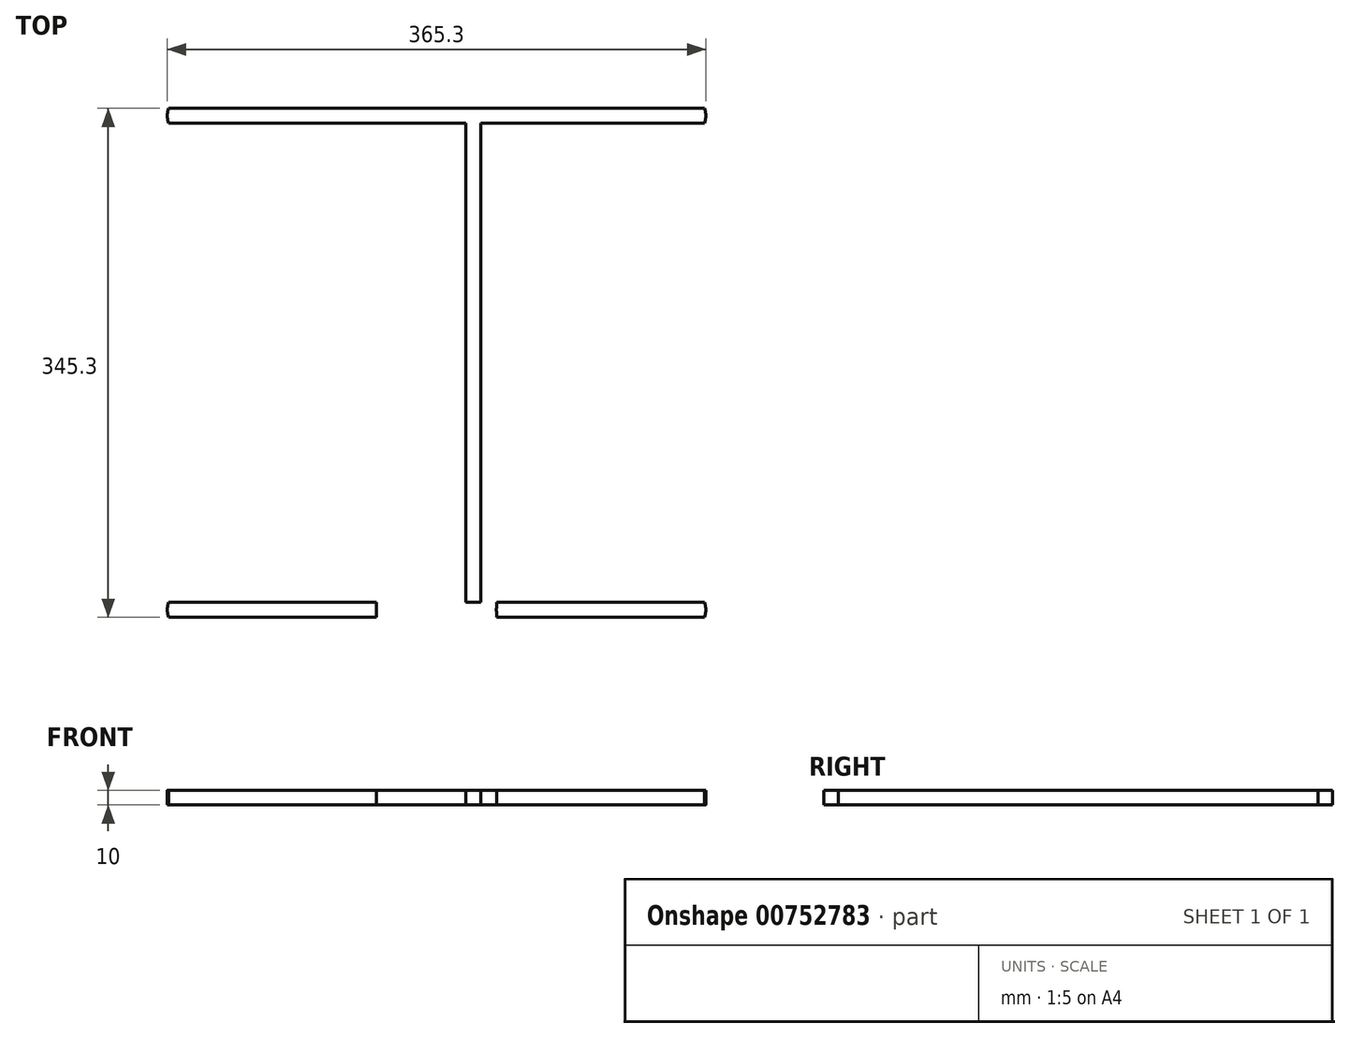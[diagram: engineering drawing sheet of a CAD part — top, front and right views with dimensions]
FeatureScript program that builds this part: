
annotation { "Feature Type Name" : "Feature", "Feature Type Description" : "" }
export const myFeature = defineFeature(function(context is Context, id is Id, definition is map)
    precondition{}
    {
        {
            var Q0;
            Q0=qCreatedBy(makeId("Top.planeOp"),FACE);
            var sketch = newSketch(context, id + "F0", { "sketchPlane" : qUnion([Q0])});
            skLineSegment(sketch, "E0.bottom", {"start": v(-30, 162.65) * mm, "end": v(30, 162.65) * mm});
            skLineSegment(sketch, "E0.top", {"start": v(-30, -162.65) * mm, "end": v(30, -162.65) * mm});
            skLineSegment(sketch, "E0.left", {"start": v(-30, 162.65) * mm, "end": v(-30, -162.65) * mm});
            skLineSegment(sketch, "E0.right", {"start": v(30, 162.65) * mm, "end": v(30, -162.65) * mm});
            skPoint(sketch, "E0.middle", {"position": v(0, 0) * mm});
            skLineSegment(sketch, "E1", {"start": v(0, 164.7) * mm, "end": v(0, 162.65) * mm, "construction": true});
            skPoint(sketch, "E1.startSnap0", {"position": v(0, 162.65) * mm});
            skPoint(sketch, "E1.endSnap0", {"position": v(0, -162.65) * mm});
            skLineSegment(sketch, "E2.bottom", {"start": v(0, 162.65) * mm, "end": v(182.65, 162.65) * mm});
            skLineSegment(sketch, "E2.top", {"start": v(0, 172.65) * mm, "end": v(182.65, 172.65) * mm});
            skLineSegment(sketch, "E2.left", {"start": v(0, 162.65) * mm, "end": v(0, 172.65) * mm});
            skLineSegment(sketch, "E2.right", {"start": v(182.65, 162.65) * mm, "end": v(182.65, 172.65) * mm});
            skLineSegment(sketch, "E3", {"start": v(-190.93, 0) * mm, "end": v(-190.22, 0) * mm, "construction": true});
            skPoint(sketch, "E3.endSnap0", {"position": v(-30, 0) * mm});
            skLineSegment(sketch, "E4.MirrorCS", {"start": v(0, 172.65) * mm, "end": v(-182.65, 172.65) * mm});
            skLineSegment(sketch, "E5.MirrorCS", {"start": v(0, 162.65) * mm, "end": v(-182.65, 162.65) * mm});
            skLineSegment(sketch, "E6.MirrorCS", {"start": v(-182.65, 162.65) * mm, "end": v(-182.65, 172.65) * mm});
            skLineSegment(sketch, "E7.MirrorCS", {"start": v(0, -172.65) * mm, "end": v(-182.65, -172.65) * mm});
            skLineSegment(sketch, "E8.MirrorCS", {"start": v(0, -162.65) * mm, "end": v(-182.65, -162.65) * mm});
            skLineSegment(sketch, "E9.MirrorCS", {"start": v(0, -172.65) * mm, "end": v(182.65, -172.65) * mm});
            skLineSegment(sketch, "E10.MirrorCS", {"start": v(0, -162.65) * mm, "end": v(182.65, -162.65) * mm});
            skLineSegment(sketch, "E11.MirrorCS", {"start": v(182.65, -162.65) * mm, "end": v(182.65, -172.65) * mm});
            skLineSegment(sketch, "E12.MirrorCS", {"start": v(-182.65, -162.65) * mm, "end": v(-182.65, -172.65) * mm});
            skLineSegment(sketch, "E13", {"start": v(170.21, 167.65) * mm, "end": v(167.65, 167.65) * mm, "construction": true});
            skCircle(sketch, "E14", {"center": v(-167.65, 167.65) * mm, "radius": 127 * mm});
            skCircle(sketch, "E15.MirrorC", {"center": v(-167.65, -167.65) * mm, "radius": 127 * mm});
            skCircle(sketch, "E16.MirrorC", {"center": v(167.65, 167.65) * mm, "radius": 127 * mm});
            skCircle(sketch, "E17.MirrorC", {"center": v(167.65, -167.65) * mm, "radius": 127 * mm});
            skLineSegment(sketch, "E18.bottom", {"start": v(-30, 162.65) * mm, "end": v(-20, 162.65) * mm});
            skLineSegment(sketch, "E18.top", {"start": v(-30, -162.65) * mm, "end": v(-20, -162.65) * mm});
            skLineSegment(sketch, "E18.right", {"start": v(-20, 162.65) * mm, "end": v(-20, -162.65) * mm});
            skLineSegment(sketch, "E19.MirrorCS", {"start": v(20, 162.65) * mm, "end": v(20, -162.65) * mm});
            skCircle(sketch, "E20", {"center": v(167.65, -167.65) * mm, "radius": 15 * mm});
            skCircle(sketch, "E21.MirrorC", {"center": v(-167.65, -167.65) * mm, "radius": 15 * mm});
            skLineSegment(sketch, "E22.MirrorCS", {"start": v(190.93, 0) * mm, "end": v(190.22, 0) * mm, "construction": true});
            skCircle(sketch, "E23.MirrorC", {"center": v(167.65, 167.65) * mm, "radius": 15 * mm});
            skCircle(sketch, "E24.MirrorC", {"center": v(-167.65, 167.65) * mm, "radius": 15 * mm});
            skLineSegment(sketch, "E25.trimOffspring", {"start": v(-30, 0) * mm, "end": v(-20, 0) * mm, "construction": true});
            skLineSegment(sketch, "E26.trimOffspring", {"start": v(20, 0) * mm, "end": v(30, 0) * mm, "construction": true});
            skLineSegment(sketch, "E27.trimOffspring", {"start": v(0, -162.65) * mm, "end": v(0, -172.65) * mm, "construction": true});
            skLineSegment(sketch, "E28.trimOffspring", {"start": v(30, 0) * mm, "end": v(20, 0) * mm, "construction": true});
            skPoint(sketch, "E29.orphan", {"position": v(0, -175.9) * mm});
            skPoint(sketch, "E30.trimOffspring.end.orphan", {"position": v(190.22, 0) * mm});
            skLineSegment(sketch, "E31.trimOffspring", {"start": v(-20, 0) * mm, "end": v(-30, 0) * mm, "construction": true});
            skLineSegment(sketch, "E32.trimOffspring", {"start": v(0, 0) * mm, "end": v(30, 0) * mm, "construction": true});
            skPoint(sketch, "E33.orphan", {"position": v(-182.65, 167.65) * mm});
            skPoint(sketch, "E34.orphan", {"position": v(182.65, 167.65) * mm});
            skLineSegment(sketch, "E35", {"start": v(0, -162.65) * mm, "end": v(0, -188.9) * mm, "construction": true});
            skCircle(sketch, "E36", {"center": v(0, 0) * mm, "radius": 238.4 * mm, "construction": true});
            skSolve(sketch);
        }
        {
            var Q0;
            {var subQ0=sQuery(id+"F0.wireOp",EDGE,"E15.MirrorC");var subQ1=sQuery(id+"F0.wireOp",EDGE,"E7.MirrorCS");var subQ2=makeQuery(id+"F0.imprint","INTERSECT",VERTEX,{"derivedFrom":[subQ1,subQ0]});Q0=makeQuery(id+"F0.imprint","IMPRINT",FACE,{"disambiguationData":[TD([[makeQuery(id+"F0.imprint","IMPRINT",EDGE,{"disambiguationData":[TD([[subQ2,-1.0]])],"derivedFrom":subQ1}),-1.0]])]});}
            var Q1;
            {var subQ8=sQuery(id+"F0.wireOp",EDGE,"E18.top");Q1=makeQuery(id+"F0.imprint","IMPRINT",FACE,{"disambiguationData":[TD([[makeQuery(id+"F0.imprint","IMPRINT",EDGE,{"derivedFrom":subQ8}),-1.0]])]});}
            var Q2;
            {var subQ0=sQuery(id+"F0.wireOp",EDGE,"E17.MirrorC");var subQ1=sQuery(id+"F0.wireOp",EDGE,"E9.MirrorCS");var subQ2=makeQuery(id+"F0.imprint","INTERSECT",VERTEX,{"derivedFrom":[subQ1,subQ0]});Q2=makeQuery(id+"F0.imprint","IMPRINT",FACE,{"disambiguationData":[TD([[makeQuery(id+"F0.imprint","IMPRINT",EDGE,{"disambiguationData":[TD([[subQ2,-1.0]])],"derivedFrom":subQ1}),1.0]])]});}
            var Q3;
            {var subQ0=sQuery(id+"F0.wireOp",EDGE,"E20");var subQ1=sQuery(id+"F0.wireOp",EDGE,"E9.MirrorCS");var subQ2=makeQuery(id+"F0.imprint","INTERSECT",VERTEX,{"disambiguationData":[OD(0.0)],"derivedFrom":[subQ1,subQ0]});Q3=makeQuery(id+"F0.imprint","IMPRINT",FACE,{"disambiguationData":[TD([[makeQuery(id+"F0.imprint","IMPRINT",EDGE,{"disambiguationData":[TD([[subQ2,-1.0]])],"derivedFrom":subQ1}),1.0]])]});}
            var Q4;
            {var subQ0=sQuery(id+"F0.wireOp",EDGE,"E21.MirrorC");var subQ1=sQuery(id+"F0.wireOp",EDGE,"E7.MirrorCS");var subQ2=makeQuery(id+"F0.imprint","INTERSECT",VERTEX,{"disambiguationData":[OD(0.0)],"derivedFrom":[subQ1,subQ0]});Q4=makeQuery(id+"F0.imprint","IMPRINT",FACE,{"disambiguationData":[TD([[makeQuery(id+"F0.imprint","IMPRINT",EDGE,{"disambiguationData":[TD([[subQ2,-1.0]])],"derivedFrom":subQ1}),-1.0]])]});}
            var Q5;
            Q5=makeQuery(id+"F0.imprint","IMPRINT",FACE,{"disambiguationData":[TD([[makeQuery(id+"F0.imprint","IMPRINT",EDGE,{"derivedFrom":sQuery(id+"F0.wireOp",EDGE,"E18.bottom")}),-1.0]])]});
            var Q6;
            {var subQ0=sQuery(id+"F0.wireOp",EDGE,"E0.right");Q6=makeQuery(id+"F0.imprint","IMPRINT",FACE,{"disambiguationData":[TD([[makeQuery(id+"F0.imprint","IMPRINT",EDGE,{"derivedFrom":subQ0}),-1.0]])]});}
            var Q7;
            {var subQ0=sQuery(id+"F0.wireOp",EDGE,"E16.MirrorC");var subQ1=sQuery(id+"F0.wireOp",EDGE,"E2.bottom");var subQ2=makeQuery(id+"F0.imprint","INTERSECT",VERTEX,{"derivedFrom":[subQ1,subQ0]});Q7=makeQuery(id+"F0.imprint","IMPRINT",FACE,{"disambiguationData":[TD([[makeQuery(id+"F0.imprint","IMPRINT",EDGE,{"disambiguationData":[TD([[subQ2,-1.0]])],"derivedFrom":subQ1}),1.0]])]});}
            var Q8;
            {var subQ4=sQuery(id+"F0.wireOp",EDGE,"E2.left");Q8=makeQuery(id+"F0.imprint","IMPRINT",FACE,{"disambiguationData":[TD([[makeQuery(id+"F0.imprint","IMPRINT",EDGE,{"derivedFrom":subQ4}),-1.0]])]});}
            var Q9;
            {var subQ1=sQuery(id+"F0.wireOp",EDGE,"E2.left");Q9=makeQuery(id+"F0.imprint","IMPRINT",FACE,{"disambiguationData":[TD([[makeQuery(id+"F0.imprint","IMPRINT",EDGE,{"derivedFrom":subQ1}),1.0]])]});}
            var Q10;
            {var subQ0=sQuery(id+"F0.wireOp",EDGE,"E14");var subQ1=sQuery(id+"F0.wireOp",EDGE,"E4.MirrorCS");var subQ2=makeQuery(id+"F0.imprint","INTERSECT",VERTEX,{"derivedFrom":[subQ1,subQ0]});Q10=makeQuery(id+"F0.imprint","IMPRINT",FACE,{"disambiguationData":[TD([[makeQuery(id+"F0.imprint","IMPRINT",EDGE,{"disambiguationData":[TD([[subQ2,-1.0]])],"derivedFrom":subQ1}),1.0]])]});}
            var Q11;
            {var subQ0=sQuery(id+"F0.wireOp",EDGE,"E24.MirrorC");var subQ1=sQuery(id+"F0.wireOp",EDGE,"E4.MirrorCS");var subQ2=makeQuery(id+"F0.imprint","INTERSECT",VERTEX,{"disambiguationData":[OD(0.0)],"derivedFrom":[subQ1,subQ0]});Q11=makeQuery(id+"F0.imprint","IMPRINT",FACE,{"disambiguationData":[TD([[makeQuery(id+"F0.imprint","IMPRINT",EDGE,{"disambiguationData":[TD([[subQ2,-1.0]])],"derivedFrom":subQ1}),1.0]])]});}
            var Q12;
            {var subQ0=sQuery(id+"F0.wireOp",EDGE,"E23.MirrorC");var subQ1=sQuery(id+"F0.wireOp",EDGE,"E2.bottom");var subQ2=makeQuery(id+"F0.imprint","INTERSECT",VERTEX,{"disambiguationData":[OD(0.0)],"derivedFrom":[subQ1,subQ0]});Q12=makeQuery(id+"F0.imprint","IMPRINT",FACE,{"disambiguationData":[TD([[makeQuery(id+"F0.imprint","IMPRINT",EDGE,{"disambiguationData":[TD([[subQ2,-1.0]])],"derivedFrom":subQ1}),1.0]])]});}
            extrude(context, id + "F1", {"entities" : qUnion([Q0, Q1, Q2, Q3, Q4, Q5, Q6, Q7, Q8, Q9, Q10, Q11, Q12]), "depth" : 10 * mm, "offsetDistance" : 25 * mm});
        }
    });
